# Revit family: Door_Sliding_DORMA_CS80-MAGNEO
name_source: partatom
category: Türen
revit_build: Autodesk Revit 2013 (Build: 20120221_2030(x64)
units: mm (PartAtom-declared; Revit-internal decimal feet)

## types (9) — shared parameters
Bauelement = L20/520
Beschreibung = CS 80 MAGNEO is an automatic operator for single-panel sliding doors
Class of protection, IP20 = Ja
Compliant with DIN 18650, ANSI, BSI = Ja
Door Overlap AB = 65 mm  [stored 0.213255 ft]
Door Overlap Au = 11 mm
Door Undercut = 10 mm  [stored 0.0328084 ft]
Funktion = Innen
Fuse protection, by others 10A = Ja
Hersteller = DORMA UK Limited
Höhe = 2100 mm
Low-energy-mode = Ja
Manufactured to ISO 9001:2000 = Ja
Material = Aluminium-Dorma Metal-Anodized Silver
Operating noise max. 55db (A) = Ja
Operator Height = 62 mm  [stored 0.203412 ft]
Operator height: with MANET single-point fixings = 62mm
Operator height: with glass clamping rail = 75mm
Operator height: with wooden door panel = 75mm
Overall depth: in-wall mounting (only operator profile) = 50mm
Overall depth: on-wall mounting (without shim plate) = 60mm
Power consumption: Automatic function max. 60W = Ja
Power consumption: Stand-by-mode 3.7W = Ja
Power supply 220-230 V AC +/- 10% 50/60 Hz = Ja
Rohbauhöhe = 2100 mm
Speed 0.2-0.6 m/s = Ja
Temperature range 0-40°C = Ja
Wandabschluss = Nach Basisbauteil
_current revision = 1
zero-valued in all types: Barcode, NominalHeight, NominalWidth, SerialNumber, TagNumber, WarrentyDuration

## per-type parameters (varying)
| type | Baugruppenkennzeichen | Breite | Door Panel | Door Panel Basepoint | Door Panel Width | Driving Path F | Manet Brackets Visible | Manet Point Width | Modell | Operator Length L | Operator length: with cover | Operator length: without cover | Operator weight in kg | Overall Length LV | Reference Line | Rohbaubreite | Typenkommentare |
| LV1 Maximum Opening 875mm - Glass Clamping Rail | C1020100 | 810 mm | DORMA_door_panel_glass_CLAMPING RAIL | 27 mm  [stored 0.0885827 ft] | 940 mm | 875 mm | Nein | 575 mm | CS80 Magneo LV1 - Glass door with clamping rail | 1750 mm  [stored 5.74147 ft] | 1840mm | 1750mm | 8.6 | 1840 mm  [stored 6.03675 ft] | 438 mm | 810 mm | Door Travel Distance maximum 875mm |
| LV2 Maximum Opening 1000mm - Glass Clamping Rail | C1020 | 935 mm | DORMA_door_panel_glass_CLAMPING RAIL | 27 mm  [stored 0.0885827 ft] | 1065 mm | 1000 mm  [stored 3.28084 ft] | Nein | 700 mm  [stored 2.29659 ft] | CS80 Magneo LV2 - Glass door with clamping rail | 2000 mm  [stored 6.56168 ft] | 2090mm | 2000mm | 9.4 | 2090 mm  [stored 6.85696 ft] | 500 mm  [stored 1.64042 ft] | 935 mm | Door Travel Distance maximum 1000mm |
| LV3 Maximum Opening 1125mm - Glass Clamping Rail | C1020 | 1060 mm  [stored 3.47769 ft] | DORMA_door_panel_glass_CLAMPING RAIL | 27 mm  [stored 0.0885827 ft] | 1190 mm | 1125 mm  [stored 3.69094 ft] | Nein | 825 mm  [stored 2.70669 ft] | CS80 Magneo LV3 - Glass door with clamping rail | 2250 mm | 2340mm | 2250mm | 10.2 | 2340 mm  [stored 7.67717 ft] | 563 mm | 1060 mm  [stored 3.47769 ft] | Door Travel Distance maximum 1125mm |
| LV1 Maximum Opening 875mm - Manet Single Point Fixing | C1020100 | 810 mm | DORMA_door_panel_glass_MANET single point fixings | 8 mm  [stored 0.0262467 ft] | 940 mm | 875 mm | Ja | 575 mm | CS80 Magneo LV1 - Manet single point fixing | 1750 mm  [stored 5.74147 ft] | 1840mm | 1750mm | 8.6 | 1840 mm  [stored 6.03675 ft] | 438 mm | 810 mm | Door Travel Distance maximum 875mm |
| LV2 Maximum Opening 1000mm - Manet Single Point Fixing | C1020 | 935 mm | DORMA_door_panel_glass_MANET single point fixings | 8 mm  [stored 0.0262467 ft] | 1065 mm | 1000 mm  [stored 3.28084 ft] | Ja | 700 mm  [stored 2.29659 ft] | CS80 Magneo LV2 - Manet single point fixing | 2000 mm  [stored 6.56168 ft] | 2090mm | 2000mm | 9.4 | 2090 mm  [stored 6.85696 ft] | 500 mm  [stored 1.64042 ft] | 935 mm | Door Travel Distance maximum 1000mm |
| LV3 Maximum Opening 1125mm - Manet Single Point Fixing | C1020 | 1060 mm  [stored 3.47769 ft] | DORMA_door_panel_glass_MANET single point fixings | 8 mm  [stored 0.0262467 ft] | 1190 mm | 1125 mm  [stored 3.69094 ft] | Ja | 700 mm  [stored 2.29659 ft] | CS80 Magneo LV2 - Manet single point fixing | 2250 mm | 2090mm | 2000mm | 9.4 | 2340 mm  [stored 7.67717 ft] | 563 mm | 1060 mm  [stored 3.47769 ft] | Door Travel Distance maximum 1000mm |
| LV3 Maximum Opening 1125mm - Solid Door Panel | C1020 | 1060 mm  [stored 3.47769 ft] | DORMA-Placeholder_Door_Panel-Solid : Solid Placeholder | 8 mm  [stored 0.0262467 ft] | 1190 mm | 1125 mm  [stored 3.69094 ft] | Nein | 700 mm  [stored 2.29659 ft] | CS80 Magneo LV2 - Solid door panel | 2250 mm | 2090mm | 2000mm | 9.4 | 2340 mm  [stored 7.67717 ft] | 563 mm | 1060 mm  [stored 3.47769 ft] | Door Travel Distance maximum 1000mm |
| LV2 Maximum Opening 1000mm - Solid Door Panel | C1020 | 935 mm | DORMA-Placeholder_Door_Panel-Solid : Solid Placeholder | 8 mm  [stored 0.0262467 ft] | 1065 mm | 1000 mm  [stored 3.28084 ft] | Nein | 700 mm  [stored 2.29659 ft] | CS80 Magneo LV2 - Solid door panel | 2000 mm  [stored 6.56168 ft] | 2090mm | 2000mm | 9.4 | 2090 mm  [stored 6.85696 ft] | 500 mm  [stored 1.64042 ft] | 935 mm | Door Travel Distance maximum 1000mm |
| LV1 Maximum Opening 875mm - Solid Door Panel | C1020100 | 810 mm | DORMA-Placeholder_Door_Panel-Solid : Solid Placeholder | 8 mm  [stored 0.0262467 ft] | 940 mm | 875 mm | Nein | 575 mm | CS80 Magneo LV1 - Solid door panel | 1750 mm  [stored 5.74147 ft] | 1840mm | 1750mm | 8.6 | 1840 mm  [stored 6.03675 ft] | 438 mm | 810 mm | Door Travel Distance maximum 875mm |

note: [stored X ft] marks values corroborated as IEEE doubles in the binary element streams (Revit-internal decimal feet)

## geometry (parser evidence)
native form markers: Sweep x15
no freeform markers — native parametric forms only
